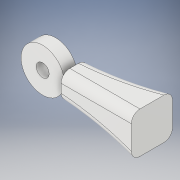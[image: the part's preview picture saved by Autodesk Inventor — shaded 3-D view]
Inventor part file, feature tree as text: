
AUTODESK INVENTOR PART (.ipt)
format: ipt  version: 2017 SP1 (Build 210196100, 196)  size: 198,656 bytes
history: native  units: in
note: dims shown in document units (in); Inventor stores cm internally (conversion verified against a paired STEP export)
features: extrude x6, sketch x6, projected_geometry x2, fillet x1
ambient origin geometry x8: Origin, YZ Plane, XZ Plane, XY Plane, X Axis, Y Axis, Z Axis, Center Point
bodies: Solid1 (feature_tree)
feature tree (15):
  extrude  "Extrusion1"  Depth=0.3937in
  extrude  "Extrusion2"  Depth=0.0394in
  extrude  "Extrusion3"  Depth=0.1181in
  extrude  "Extrusion4"  Depth=0.2362in
  extrude  "Extrusion5"  Depth=0.374in
  extrude  "Extrusion6"  Depth=5.9055in
  fillet  "Fillet1"  Radius=0.2362in
  sketch  "Sketch1"  dims[d0=0.1181in d1=0.3937in]
  sketch  "Sketch2"  dims[d2=0.1181in d3=0.0in d4=0.0394in]
  sketch  "Sketch3"  dims[d6=0.1181in d7=0.0in d8=0.1181in]
  sketch  "Sketch4"  dims[d9=0.2362in d10=0.2362in]
  sketch  "Sketch5"  dims[d11=0.7087in d12=0.0in d13=0.374in]
  sketch  "Sketch6"  dims[d14=5.9055in d15=5.9055in d16=0.2362in d17=0.0in d18=0.374in d19=5.9055in d20=5.9055in d21=0.128in d22=0.2461in d23=0.0in d24=0.0in d25=0.128in d26=0.0in d27=0.0787in]
  projected_geometry  "Projected Loop1"
  projected_geometry  "Projected Loop2"
